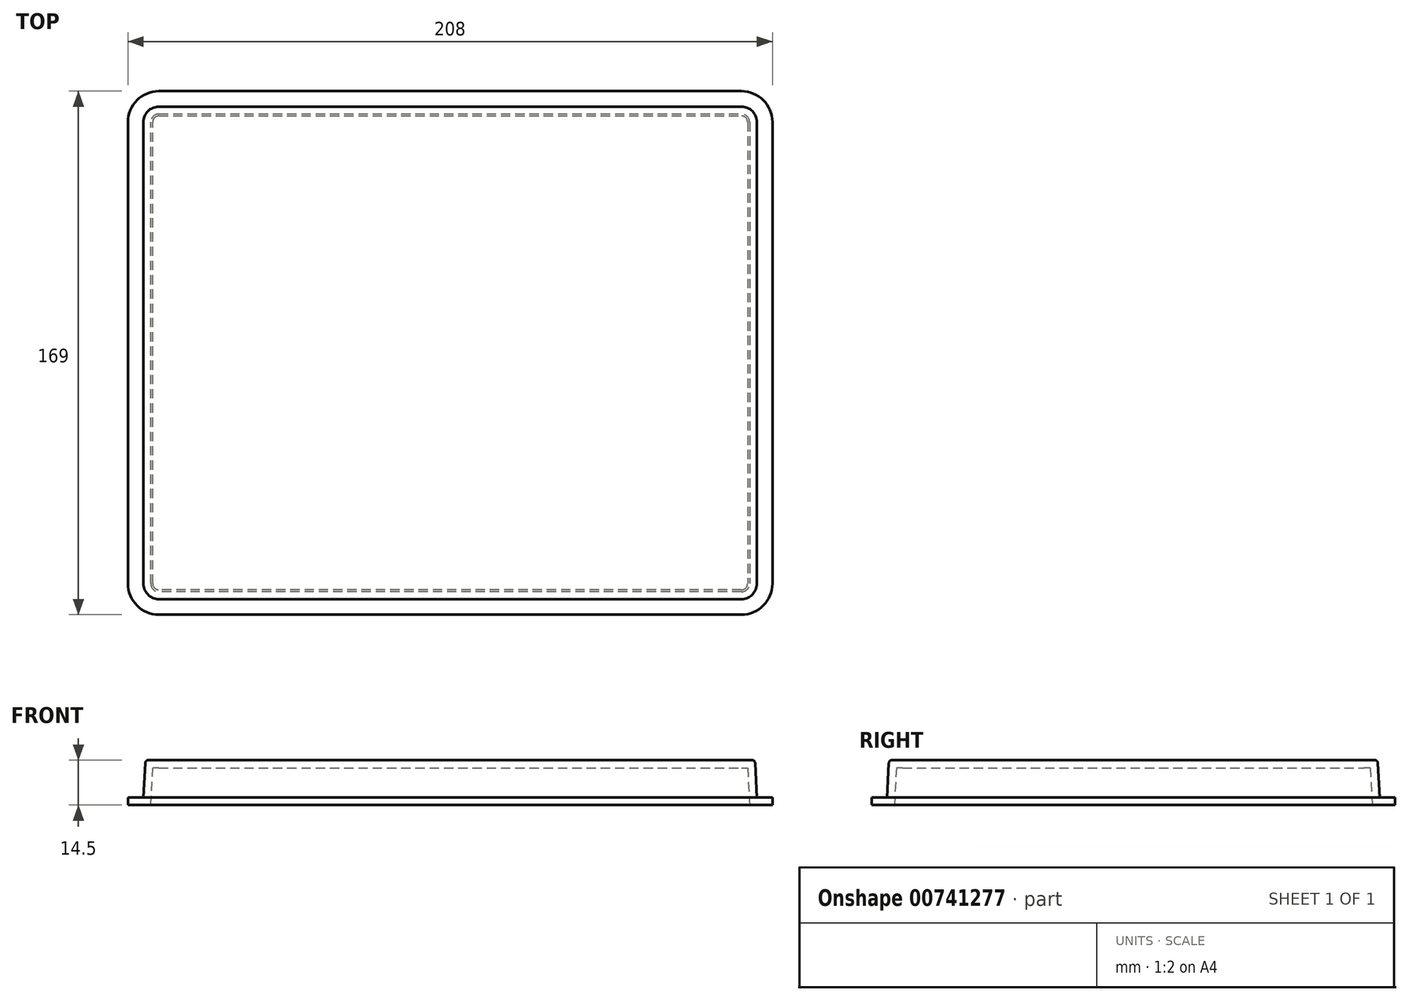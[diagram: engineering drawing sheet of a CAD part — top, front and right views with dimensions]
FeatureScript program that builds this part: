
annotation { "Feature Type Name" : "Feature", "Feature Type Description" : "" }
export const myFeature = defineFeature(function(context is Context, id is Id, definition is map)
    precondition{}
    {
        {
            var Q0;
            Q0=qCreatedBy(makeId("Top.planeOp"),FACE);
            var sketch = newSketch(context, id + "F0", { "sketchPlane" : qUnion([Q0])});
            skLineSegment(sketch, "E0.bottom", {"start": v(94, 79.5) * mm, "end": v(-94, 79.5) * mm});
            skLineSegment(sketch, "E0.top", {"start": v(94, -79.5) * mm, "end": v(-94, -79.5) * mm});
            skLineSegment(sketch, "E0.left", {"start": v(99, 74.5) * mm, "end": v(99, -74.5) * mm});
            skLineSegment(sketch, "E0.right", {"start": v(-99, 74.5) * mm, "end": v(-99, -74.5) * mm});
            skPoint(sketch, "E0.middle", {"position": v(0, 0) * mm});
            skPoint(sketch, "E1.visualSharp", {"position": v(99, 79.5) * mm});
            skArc(sketch, "E1.filletArc", {"start": v(99, 74.5) * mm, "mid": v(97.54, 78.04) * mm, "end": v(94, 79.5) * mm});
            skPoint(sketch, "E2.visualSharp", {"position": v(-99, 79.5) * mm});
            skArc(sketch, "E2.filletArc", {"start": v(-94, 79.5) * mm, "mid": v(-97.54, 78.04) * mm, "end": v(-99, 74.5) * mm});
            skPoint(sketch, "E3.visualSharp", {"position": v(-99, -79.5) * mm});
            skArc(sketch, "E3.filletArc", {"start": v(-99, -74.5) * mm, "mid": v(-97.54, -78.04) * mm, "end": v(-94, -79.5) * mm});
            skPoint(sketch, "E4.visualSharp", {"position": v(99, -79.5) * mm});
            skArc(sketch, "E4.filletArc", {"start": v(94, -79.5) * mm, "mid": v(97.54, -78.04) * mm, "end": v(99, -74.5) * mm});
            skSolve(sketch);
        }
        {
            var Q0;
            Q0 = qSketchRegion(id + "F0", true);
            extrude(context, id + "F1", {"entities" : qUnion([Q0]), "depth" : 12 * mm, "offsetDistance" : 25 * mm, "hasDraft" : true, "draftAngle" : 3 * degree, "draftPullDirection" : true});
        }
        {
            var Q0;
            Q0=makeQuery(id+"F1.opExtrude","CAP_FACE",FACE,{"disambiguationData":[OSD([sQuery(id+"F0.wireOp",EDGE,"E0.bottom"),sQuery(id+"F0.wireOp",EDGE,"E0.top"),sQuery(id+"F0.wireOp",EDGE,"E0.left"),sQuery(id+"F0.wireOp",EDGE,"E0.right"),sQuery(id+"F0.wireOp",EDGE,"E1.filletArc"),sQuery(id+"F0.wireOp",EDGE,"E2.filletArc"),sQuery(id+"F0.wireOp",EDGE,"E3.filletArc"),sQuery(id+"F0.wireOp",EDGE,"E4.filletArc")])],"isStart":true});
            var sketch = newSketch(context, id + "F2", { "sketchPlane" : qUnion([Q0])});
            skArc(sketch, "E5.0", {"start": v(104, 74.5) * mm, "mid": v(101.07, 81.57) * mm, "end": v(94, 84.5) * mm});
            skLineSegment(sketch, "E5.1", {"start": v(104, -74.5) * mm, "end": v(104, 74.5) * mm});
            skLineSegment(sketch, "E5.2", {"start": v(94, 84.5) * mm, "end": v(-94, 84.5) * mm});
            skArc(sketch, "E5.3", {"start": v(94, -84.5) * mm, "mid": v(101.07, -81.57) * mm, "end": v(104, -74.5) * mm});
            skArc(sketch, "E5.4", {"start": v(-94, 84.5) * mm, "mid": v(-101.07, 81.57) * mm, "end": v(-104, 74.5) * mm});
            skLineSegment(sketch, "E5.5", {"start": v(-104, -74.5) * mm, "end": v(-104, 74.5) * mm});
            skArc(sketch, "E5.6", {"start": v(-104, -74.5) * mm, "mid": v(-101.07, -81.57) * mm, "end": v(-94, -84.5) * mm});
            skLineSegment(sketch, "E5.7", {"start": v(94, -84.5) * mm, "end": v(-94, -84.5) * mm});
            skSolve(sketch);
        }
        {
            var Q0;
            Q0 = qSketchRegion(id + "F2", true);
            extrude(context, id + "F3", {"entities" : qUnion([Q0]), "operationType" : NewBodyOperationType.ADD, "depth" : 2.5 * mm, "offsetDistance" : 25 * mm});
        }
        {
            var Q0;
            Q0=makeQuery(id+"F1.opExtrude","CAP_FACE",FACE,{"disambiguationData":[OSD([sQuery(id+"F0.wireOp",EDGE,"E0.bottom"),sQuery(id+"F0.wireOp",EDGE,"E0.top"),sQuery(id+"F0.wireOp",EDGE,"E0.left"),sQuery(id+"F0.wireOp",EDGE,"E0.right"),sQuery(id+"F0.wireOp",EDGE,"E1.filletArc"),sQuery(id+"F0.wireOp",EDGE,"E2.filletArc"),sQuery(id+"F0.wireOp",EDGE,"E3.filletArc"),sQuery(id+"F0.wireOp",EDGE,"E4.filletArc")])],"isStart":false});
            fillet(context, id + "F4", {"entities" : qUnion([Q0]), "radius" : 1 * mm, "tangentPropagation" : true, "allowEdgeOverflow" : false});
        }
        {
            var Q0;
            Q0=makeQuery(id+"F3.opExtrude","CAP_FACE",FACE,{"disambiguationData":[OSD([sQuery(id+"F2.wireOp",EDGE,"E5.0"),sQuery(id+"F2.wireOp",EDGE,"E5.1"),sQuery(id+"F2.wireOp",EDGE,"E5.2"),sQuery(id+"F2.wireOp",EDGE,"E5.3"),sQuery(id+"F2.wireOp",EDGE,"E5.4"),sQuery(id+"F2.wireOp",EDGE,"E5.5"),sQuery(id+"F2.wireOp",EDGE,"E5.6"),sQuery(id+"F2.wireOp",EDGE,"E5.7")])],"isStart":false});
            shell(context, id + "F5", {"entities" : qUnion([Q0]), "thickness" : 2.5 * mm});
        }
    });
